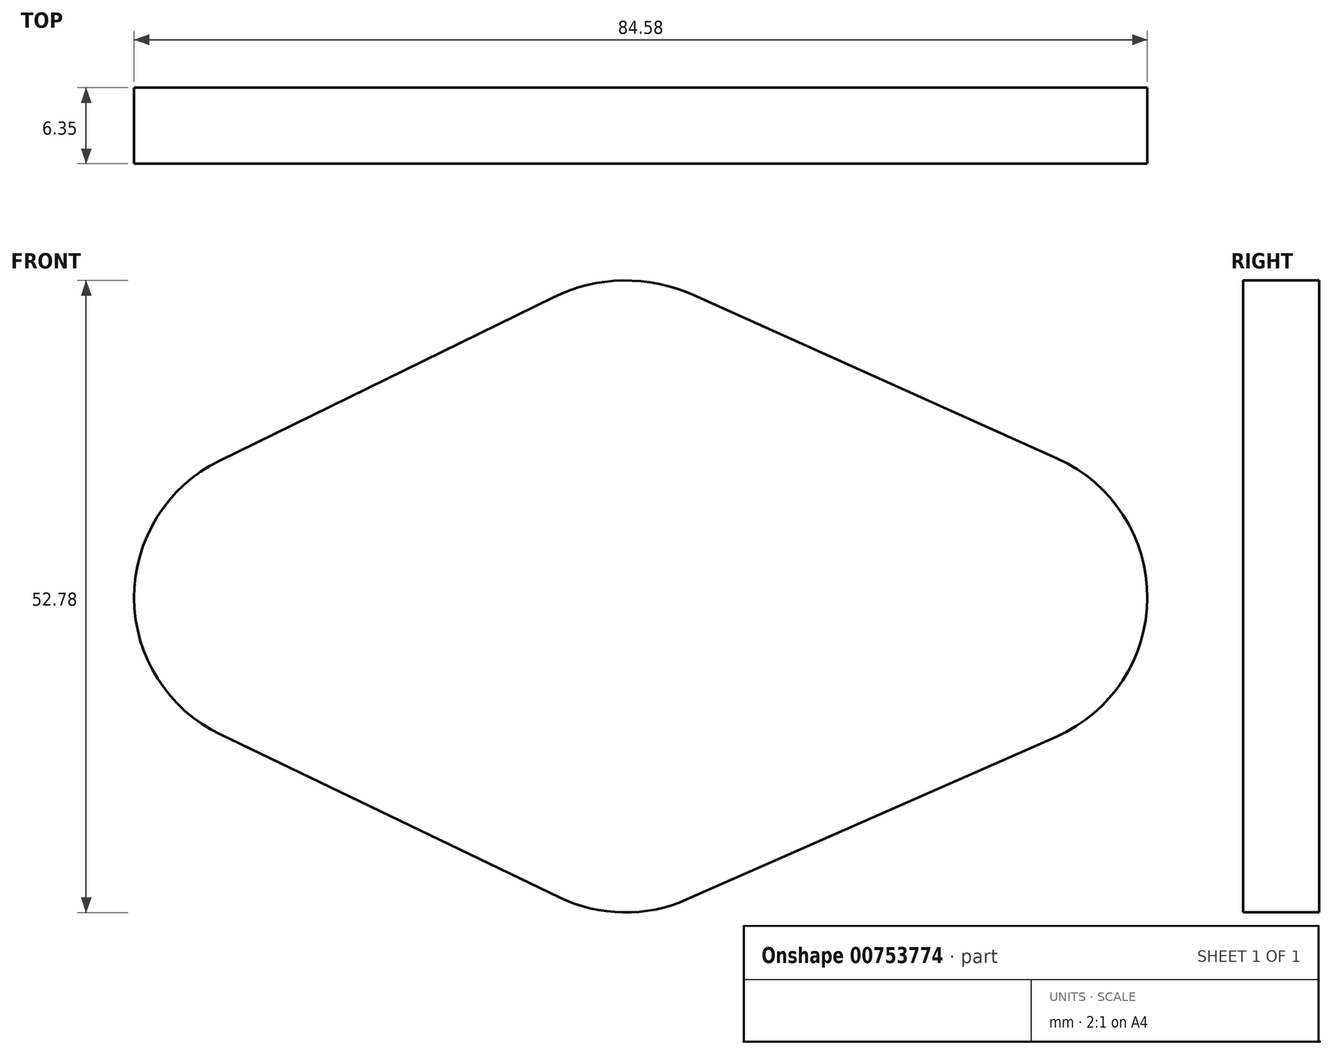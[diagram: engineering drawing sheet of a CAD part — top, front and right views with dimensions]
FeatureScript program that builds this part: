
annotation { "Feature Type Name" : "Feature", "Feature Type Description" : "" }
export const myFeature = defineFeature(function(context is Context, id is Id, definition is map)
    precondition{}
    {
        {
            var Q0;
            Q0=qCreatedBy(makeId("Front.planeOp"),FACE);
            var sketch = newSketch(context, id + "F0", { "sketchPlane" : qUnion([Q0])});
            skLineSegment(sketch, "E0", {"start": v(-33.67, 11.51) * mm, "end": v(-5.8, 25.16) * mm});
            skLineSegment(sketch, "E1", {"start": v(5.9, 25.36) * mm, "end": v(36.3, 11.7) * mm});
            skLineSegment(sketch, "E2", {"start": v(-33.58, -11.34) * mm, "end": v(-5.27, -24.95) * mm});
            skLineSegment(sketch, "E3", {"start": v(5.35, -25.13) * mm, "end": v(36.22, -11.51) * mm});
            skPoint(sketch, "E4.visualSharp", {"position": v(0, 28) * mm});
            skArc(sketch, "E4.filletArc", {"start": v(5.9, 25.36) * mm, "mid": v(0.02, 26.56) * mm, "end": v(-5.8, 25.16) * mm});
            skPoint(sketch, "E5.visualSharp", {"position": v(0, -27.49) * mm});
            skArc(sketch, "E5.filletArc", {"start": v(-5.27, -24.95) * mm, "mid": v(0.02, -26.2) * mm, "end": v(5.35, -25.13) * mm});
            skPoint(sketch, "E6.visualSharp", {"position": v(62.33, 0) * mm});
            skArc(sketch, "E6.filletArc", {"start": v(36.22, -11.51) * mm, "mid": v(43.8, 0.06) * mm, "end": v(36.3, 11.7) * mm});
            skPoint(sketch, "E7.visualSharp", {"position": v(-57.17, 0) * mm});
            skArc(sketch, "E7.filletArc", {"start": v(-33.67, 11.51) * mm, "mid": v(-40.78, 0.06) * mm, "end": v(-33.58, -11.34) * mm});
            skSolve(sketch);
        }
        {
            var Q0;
            Q0=makeQuery(id+"F0.imprint","IMPRINT",FACE,{"disambiguationData":[TD([[makeQuery(id+"F0.imprint","IMPRINT",EDGE,{"derivedFrom":sQuery(id+"F0.wireOp",EDGE,"E0")}),-1.0]])]});
            extrude(context, id + "F1", {"entities" : qUnion([Q0]), "depth" : 6.35 * mm, "offsetDistance" : 25.4 * mm});
        }
    });
